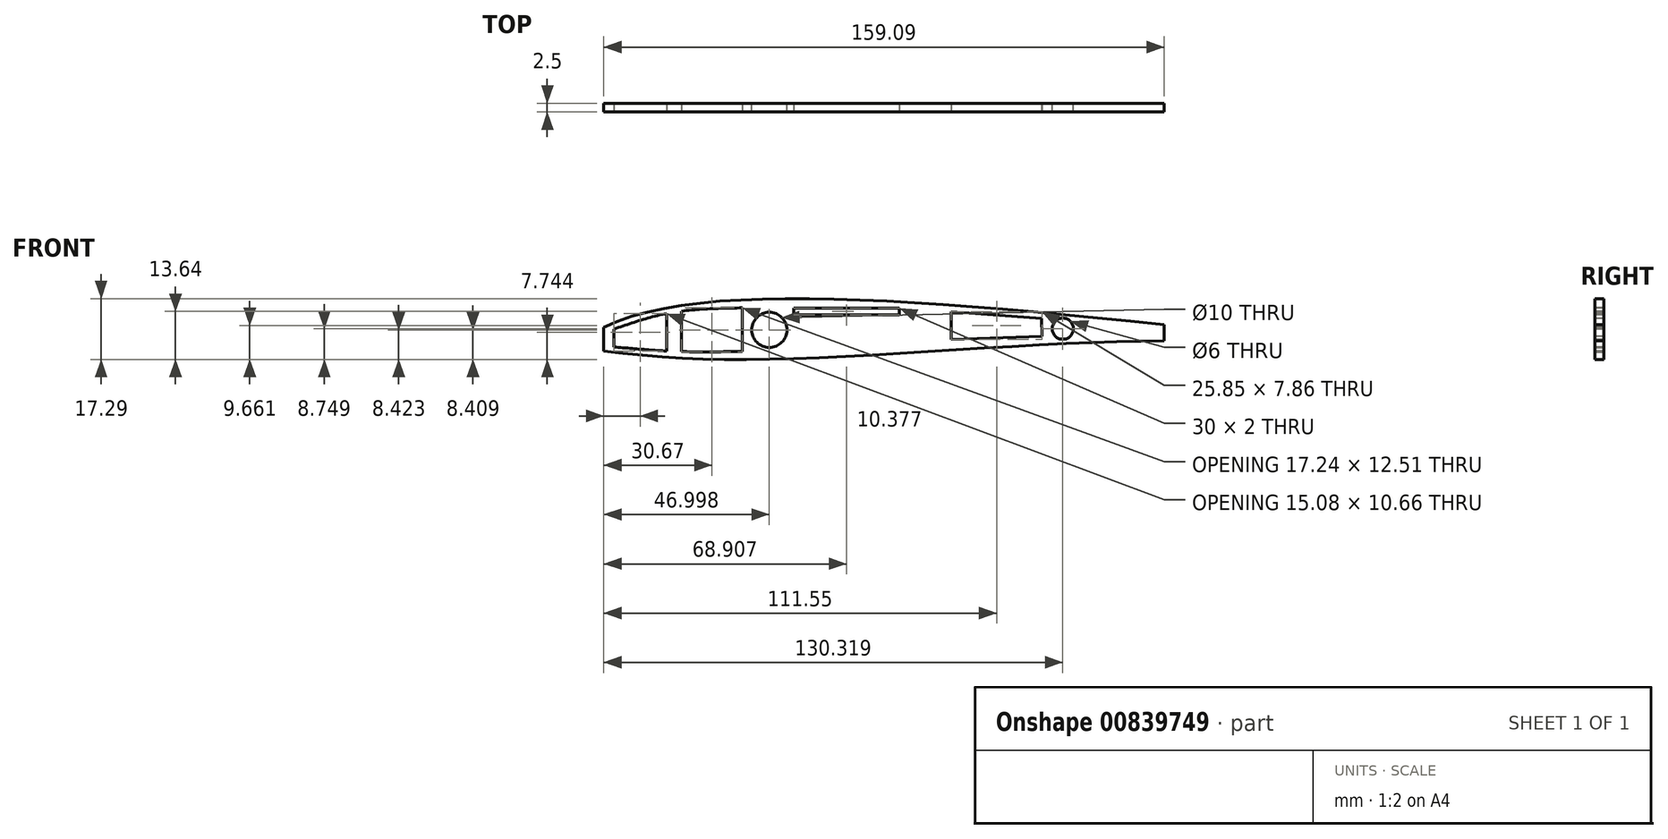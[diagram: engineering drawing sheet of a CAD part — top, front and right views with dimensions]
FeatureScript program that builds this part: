
annotation { "Feature Type Name" : "Feature", "Feature Type Description" : "" }
export const myFeature = defineFeature(function(context is Context, id is Id, definition is map)
    precondition{}
    {
        {
            var Q0;
            Q0=qCreatedBy(makeId("Front.planeOp"),FACE);
            var sketch = newSketch(context, id + "F0", { "sketchPlane" : qUnion([Q0])});
            skPoint(sketch, "E0.middle", {"position": v(0, 0) * mm});
            skLineSegment(sketch, "E1", {"start": v(-99.95, -4.05) * mm, "end": v(-99.64, -4.05) * mm});
            skFitSpline(sketch, "E2", {"points": [v(-96.98, -0.81) * mm, v(-45.24, 7.5) * mm, v(100, -4.05) * mm], "startDerivative": vector(97.58, 47.67) * mm, "endDerivative": vector(275.05, -31.29) * mm});
            skFitSpline(sketch, "E3", {"points": [v(-96.54, -7.34) * mm, v(-44.56, -9.6) * mm, v(41.7, -4.97) * mm, v(100, -4.05) * mm], "startDerivative": vector(159.07, -20.98) * mm, "endDerivative": vector(169.88, 6) * mm});
            skFitSpline(sketch, "E4", {"points": [v(-96.54, -7.34) * mm, v(-101.41, -5) * mm, v(-96.98, -0.81) * mm], "startDerivative": vector(-18.7, 3.9) * mm, "endDerivative": vector(17.62, 9.13) * mm});
            skArc(sketch, "E5.trimOffspring", {"start": v(-97.54, -7.12) * mm, "mid": v(-97.05, -7.27) * mm, "end": v(-96.54, -7.34) * mm});
            skFitSpline(sketch, "E6", {"points": [v(-96.34, -1.64) * mm, v(-45.34, 6.27) * mm, v(86.1, -3.38) * mm], "startDerivative": vector(82.57, 38.4) * mm, "endDerivative": vector(239.73, -24.74) * mm});
            skFitSpline(sketch, "E7", {"points": [v(-97.38, -6.05) * mm, v(-44.49, -7.96) * mm, v(41.39, -3.9) * mm, v(86.1, -3.38) * mm], "startDerivative": vector(144.05, -26.77) * mm, "endDerivative": vector(139.27, -2.3) * mm});
            skFitSpline(sketch, "E8", {"points": [v(-97.38, -6.05) * mm, v(-99.95, -4.56) * mm, v(-96.34, -1.64) * mm], "startDerivative": vector(-8.62, 1.03) * mm, "endDerivative": vector(10.24, 4.38) * mm});
            skSolve(sketch);
        }
        {
            var Q0;
            Q0=qCreatedBy(makeId("Front.planeOp"),FACE);
            var sketch = newSketch(context, id + "F1", { "sketchPlane" : qUnion([Q0])});
            skLineSegment(sketch, "E9", {"start": v(-109.84, -5.04) * mm, "end": v(108.45, -3.99) * mm});
            skCircle(sketch, "E10", {"center": v(-49.54, -1.37) * mm, "radius": 5 * mm});
            skCircle(sketch, "E11", {"center": v(33.78, -1.03) * mm, "radius": 3 * mm});
            skSolve(sketch);
        }
        {
            var Q0;
            {var subQ0=sQuery(id+"F0.wireOp",EDGE,"E6");Q0=makeQuery(id+"F0.imprint","IMPRINT",FACE,{"disambiguationData":[TD([[makeQuery(id+"F0.imprint","IMPRINT",EDGE,{"derivedFrom":subQ0}),-1.0]])]});}
            var Q1;
            {var subQ1=sQuery(id+"F0.wireOp",EDGE,"E2");Q1=makeQuery(id+"F0.imprint","IMPRINT",FACE,{"disambiguationData":[TD([[makeQuery(id+"F0.imprint","IMPRINT",EDGE,{"derivedFrom":subQ1}),-1.0]])]});}
            var Q2;
            Q2=makeQuery(id+"F1.imprint","IMPRINT",FACE,{"disambiguationData":[TD([[makeQuery(id+"F1.imprint","IMPRINT",EDGE,{"derivedFrom":sQuery(id+"F1.wireOp",EDGE,"E11")}),1.0]])]});
            var Q3;
            {var subQ0=sQuery(id+"F1.wireOp",EDGE,"E10");var subQ1=sQuery(id+"F1.wireOp",EDGE,"E9");var subQ2=makeQuery(id+"F1.imprint","INTERSECT",VERTEX,{"disambiguationData":[OD(0.0)],"derivedFrom":[subQ1,subQ0]});Q3=makeQuery(id+"F1.imprint","IMPRINT",FACE,{"disambiguationData":[TD([[makeQuery(id+"F1.imprint","IMPRINT",EDGE,{"disambiguationData":[TD([[subQ2,-1.0]])],"derivedFrom":subQ1}),1.0]])]});}
            var Q4;
            {var subQ0=sQuery(id+"F1.wireOp",EDGE,"E10");var subQ1=sQuery(id+"F1.wireOp",EDGE,"E9");var subQ2=makeQuery(id+"F1.imprint","INTERSECT",VERTEX,{"disambiguationData":[OD(0.0)],"derivedFrom":[subQ1,subQ0]});Q4=makeQuery(id+"F1.imprint","IMPRINT",FACE,{"disambiguationData":[TD([[makeQuery(id+"F1.imprint","IMPRINT",EDGE,{"disambiguationData":[TD([[subQ2,-1.0]])],"derivedFrom":subQ1}),-1.0]])]});}
            var Q5;
            {var subQ0=sQuery(id+"F0.wireOp",EDGE,"E5.trimOffspring");Q5=makeQuery(id+"F0.imprint","IMPRINT",FACE,{"disambiguationData":[TD([[makeQuery(id+"F0.imprint","IMPRINT",EDGE,{"derivedFrom":subQ0}),1.0]])]});}
            extrude(context, id + "F2", {"entities" : qUnion([Q0, Q1, Q2, Q3, Q4, Q5]), "depth" : 2.5 * mm, "offsetDistance" : 25 * mm});
        }
        {
            var Q0;
            Q0=qSketchRegion(id+"F1",true);
            var Q1;
            Q1=sQuery(id+"F1.wireOp",EDGE,"E11");
            var Q2;
            Q2=sQuery(id+"F1.wireOp",EDGE,"E10");
            extrude(context, id + "F3", {"entities" : qUnion([Q0]), "operationType" : NewBodyOperationType.REMOVE, "surfaceEntities" : qUnion([Q1, Q2]), "depth" : 2.5 * mm, "offsetDistance" : 25 * mm});
        }
        {
            var Q0;
            Q0=makeQuery(id+"F2.opExtrude","CAP_FACE",FACE,{"disambiguationData":[OSD([sQuery(id+"F0.wireOp",EDGE,"E2"),sQuery(id+"F0.wireOp",EDGE,"E3"),sQuery(id+"F0.wireOp",EDGE,"E4"),sQuery(id+"F0.wireOp",EDGE,"E5.trimOffspring")])],"isStart":false});
            var sketch = newSketch(context, id + "F4", { "sketchPlane" : qUnion([Q0])});
            skLineSegment(sketch, "E12", {"start": v(-96.54, -0.6) * mm, "end": v(-96.54, -7.34) * mm});
            skPoint(sketch, "E13.end.orphan", {"position": v(-96.98, -7.34) * mm});
            skLineSegment(sketch, "E14", {"start": v(-57.25, 4.9) * mm, "end": v(-57.25, -7.48) * mm});
            skFitSpline(sketch, "E15", {"points": [v(-57.25, -7.48) * mm, v(-75.97, -7.48) * mm, v(-93.7, -6.2) * mm], "startDerivative": vector(-37.23, -0.66) * mm, "endDerivative": vector(-35.67, 3.25) * mm});
            skFitSpline(sketch, "E16", {"points": [v(-57.25, 4.9) * mm, v(-77.46, 3.51) * mm, v(-93.7, -1.14) * mm], "startDerivative": vector(-39.88, -0.8) * mm, "endDerivative": vector(-32.92, -11.45) * mm});
            skLineSegment(sketch, "E17", {"start": v(-93.7, -1.14) * mm, "end": v(-93.7, -6.2) * mm});
            skLineSegment(sketch, "E18", {"start": v(2.08, 3.8) * mm, "end": v(2.08, -4.05) * mm});
            skLineSegment(sketch, "E19", {"start": v(2.08, -4.05) * mm, "end": v(27.94, -3.22) * mm});
            skLineSegment(sketch, "E20", {"start": v(27.94, -3.22) * mm, "end": v(27.77, 1.91) * mm});
            skLineSegment(sketch, "E21", {"start": v(27.77, 1.91) * mm, "end": v(2.08, 3.8) * mm});
            skLineSegment(sketch, "E22", {"start": v(-78.62, 3.3) * mm, "end": v(-78.62, -7.37) * mm});
            skLineSegment(sketch, "E23", {"start": v(-74.49, 3.96) * mm, "end": v(-74.49, -7.53) * mm});
            skPoint(sketch, "E24.end.orphan", {"position": v(-41.2, -6.73) * mm});
            skLineSegment(sketch, "E25.bottom", {"start": v(-42.63, 4.86) * mm, "end": v(-12.63, 4.86) * mm});
            skLineSegment(sketch, "E25.top", {"start": v(-42.63, 2.86) * mm, "end": v(-12.63, 2.86) * mm});
            skLineSegment(sketch, "E25.left", {"start": v(-42.63, 4.86) * mm, "end": v(-42.63, 2.86) * mm});
            skLineSegment(sketch, "E25.right", {"start": v(-12.63, 4.86) * mm, "end": v(-12.63, 2.86) * mm});
            skLineSegment(sketch, "E26", {"start": v(62.55, 0.1) * mm, "end": v(62.55, -4.52) * mm});
            skSolve(sketch);
        }
        {
            var Q0;
            {var subQ0=sQuery(id+"F4.wireOp",EDGE,"E12");Q0=makeQuery(id+"F4.imprint","IMPRINT",FACE,{"disambiguationData":[TD([[makeQuery(id+"F4.imprint","IMPRINT",EDGE,{"derivedFrom":subQ0}),-1.0]])]});}
            extrude(context, id + "F5", {"entities" : qUnion([Q0]), "operationType" : NewBodyOperationType.REMOVE, "oppositeDirection" : true, "depth" : 2.5 * mm, "offsetDistance" : 25 * mm});
        }
        {
            var Q0;
            Q0=makeQuery(id+"F4.imprint","IMPRINT",FACE,{"disambiguationData":[TD([[makeQuery(id+"F4.imprint","IMPRINT",EDGE,{"derivedFrom":sQuery(id+"F4.wireOp",EDGE,"E17")}),1.0]])]});
            var Q1;
            Q1=makeQuery(id+"F4.imprint","IMPRINT",FACE,{"disambiguationData":[TD([[makeQuery(id+"F4.imprint","IMPRINT",EDGE,{"derivedFrom":sQuery(id+"F4.wireOp",EDGE,"E14")}),-1.0]])]});
            var Q2;
            Q2=makeQuery(id+"F4.imprint","IMPRINT",FACE,{"disambiguationData":[TD([[makeQuery(id+"F4.imprint","IMPRINT",EDGE,{"derivedFrom":sQuery(id+"F4.wireOp",EDGE,"E25.bottom")}),-1.0]])]});
            var Q3;
            Q3=makeQuery(id+"F4.imprint","IMPRINT",FACE,{"disambiguationData":[TD([[makeQuery(id+"F4.imprint","IMPRINT",EDGE,{"derivedFrom":sQuery(id+"F4.wireOp",EDGE,"E18")}),1.0]])]});
            extrude(context, id + "F6", {"entities" : qUnion([Q0, Q1, Q2, Q3]), "operationType" : NewBodyOperationType.REMOVE, "oppositeDirection" : true, "depth" : 2.5 * mm, "offsetDistance" : 25 * mm});
        }
        {
            var Q0;
            {var subQ0=sQuery(id+"F4.wireOp",EDGE,"E26");Q0=makeQuery(id+"F4.imprint","IMPRINT",FACE,{"disambiguationData":[TD([[makeQuery(id+"F4.imprint","IMPRINT",EDGE,{"derivedFrom":subQ0}),1.0]])]});}
            extrude(context, id + "F7", {"entities" : qUnion([Q0]), "operationType" : NewBodyOperationType.REMOVE, "oppositeDirection" : true, "depth" : 2.5 * mm, "offsetDistance" : 25 * mm});
        }
    });
